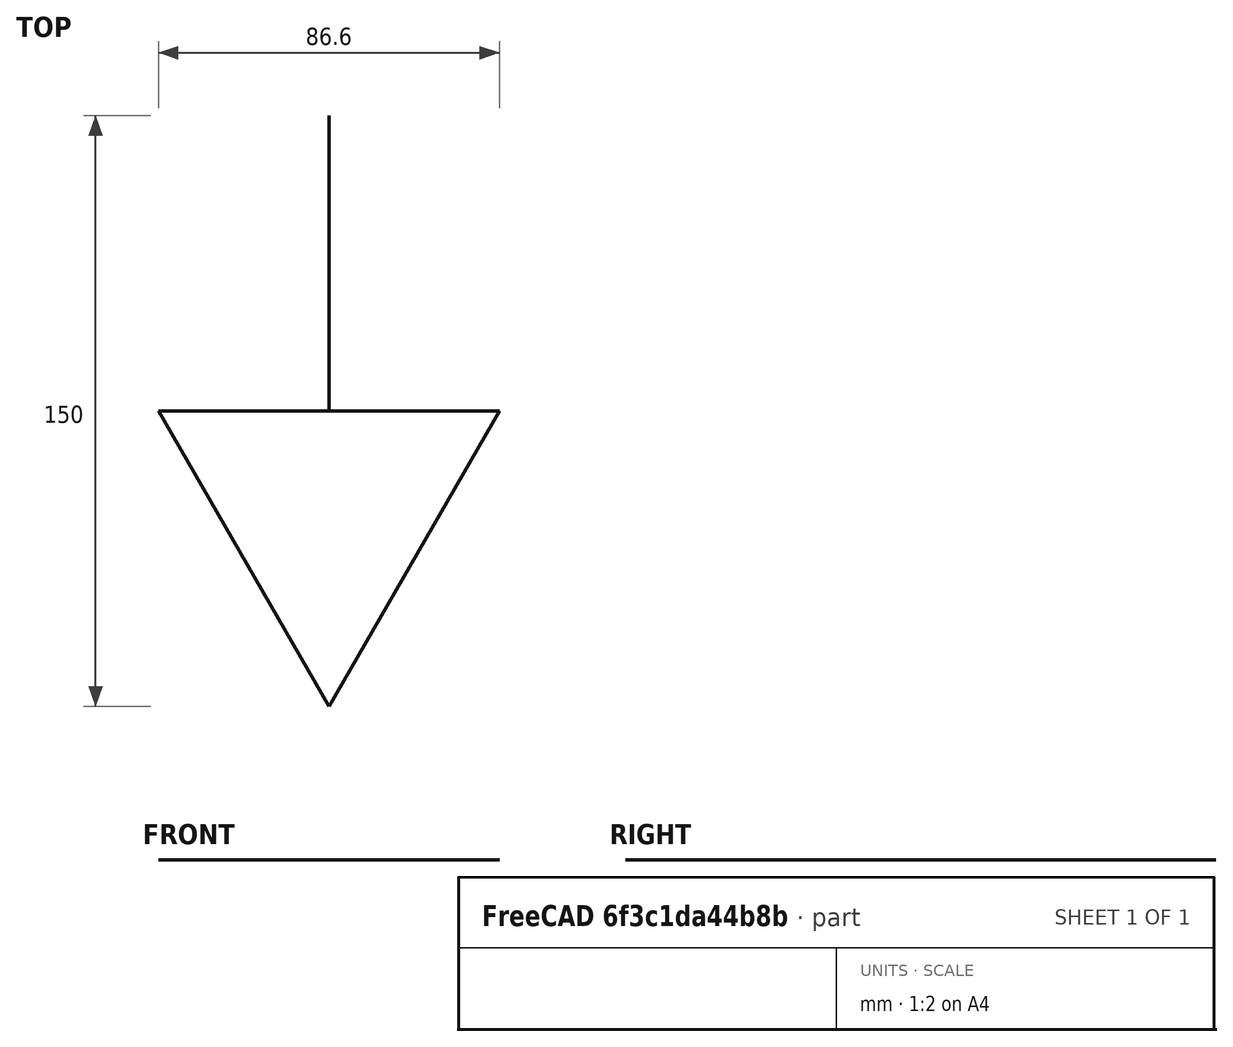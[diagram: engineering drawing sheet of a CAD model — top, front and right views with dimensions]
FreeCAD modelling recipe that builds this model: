
FCSTD DOCUMENT  (FreeCAD 1.1R20260325 (Git shallow))
Label: Tomada_Alta_1modulo_220v_com_simbologia
License: All rights reserved
LicenseURL: http://en.wikipedia.org/wiki/All_rights_reserved
objects: Part::FeaturePython×1, Part::Feature×1, App::DocumentObjectGroup×1
note: 2 computed .brp shape members not serialized (recipe doc carries the construction recipe); baked Part::Feature solids carry a one-line shape summary decoded from their .brp

FEATURE [Part::FeaturePython] Component  label="Tomada_1modulo_110v_alta"  # Arch/BIM 0 (typed FeaturePython)
  HorizontalArea = 0
  IfcData = attributes={"GlobalId": {"name": "GlobalId", "type": "IfcGloballyUniqueId", "is_enum": false, "enum_values": []}, "Description": {"... (+538 chars omitted),+1 more (map truncated)
  IfcType = 0
  MoveBase = false
  MoveWithHost = false
  PerimeterLength = 0
  Placement = pos=(0,0,2250) rot=(0,0,1;0rad)
  PredefinedType = 0
  VerticalArea = 0
FEATURE [Part::Feature] Compound002002002004005002002003003002003005002002005002002002002002002001  label="Simbologia_tomada_alta"
  Placement = pos=(1045.43,2054.32,2240.37) rot=(0,0,-1;1.5708rad)
  shape: bbox 86.6 x 150 x 2e-07 mm, 1 faces, 0 solids (baked)
FEATURE [App::DocumentObjectGroup] Group  label="Tomada_Alta"
  Group = -> [Component,Compound002002002004005002002003003002003005002002005002002002002002002001]
